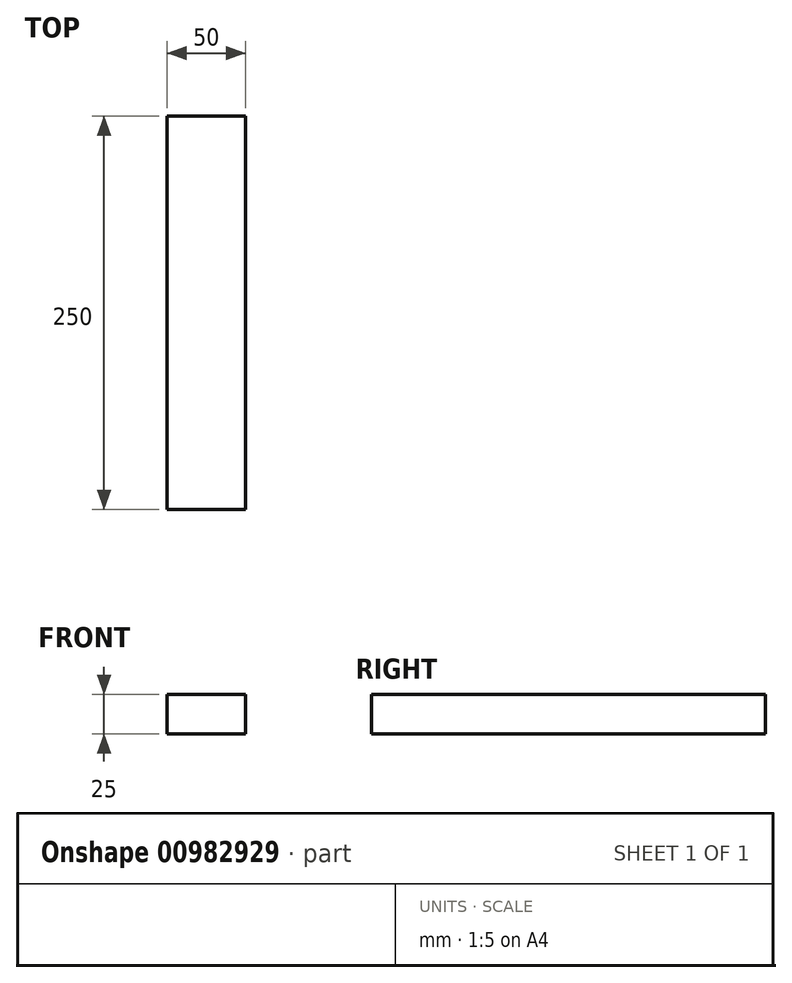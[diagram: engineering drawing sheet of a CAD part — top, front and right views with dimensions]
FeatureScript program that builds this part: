
annotation { "Feature Type Name" : "Feature", "Feature Type Description" : "" }
export const myFeature = defineFeature(function(context is Context, id is Id, definition is map)
    precondition{}
    {
        {
            var Q0;
            Q0=qCreatedBy(makeId("Front.planeOp"),FACE);
            var sketch = newSketch(context, id + "F0", { "sketchPlane" : qUnion([Q0])});
            skLineSegment(sketch, "E0.bottom", {"start": v(-25, 0) * mm, "end": v(25, 0) * mm});
            skLineSegment(sketch, "E0.top", {"start": v(-25, 25) * mm, "end": v(25, 25) * mm});
            skLineSegment(sketch, "E0.left", {"start": v(-25, 0) * mm, "end": v(-25, 25) * mm});
            skLineSegment(sketch, "E0.right", {"start": v(25, 0) * mm, "end": v(25, 25) * mm});
            skSolve(sketch);
        }
        {
            var Q0;
            Q0 = qSketchRegion(id + "F0", true);
            extrude(context, id + "F1", {"entities" : qUnion([Q0]), "depth" : 250 * mm, "offsetDistance" : 25 * mm});
        }
    });
